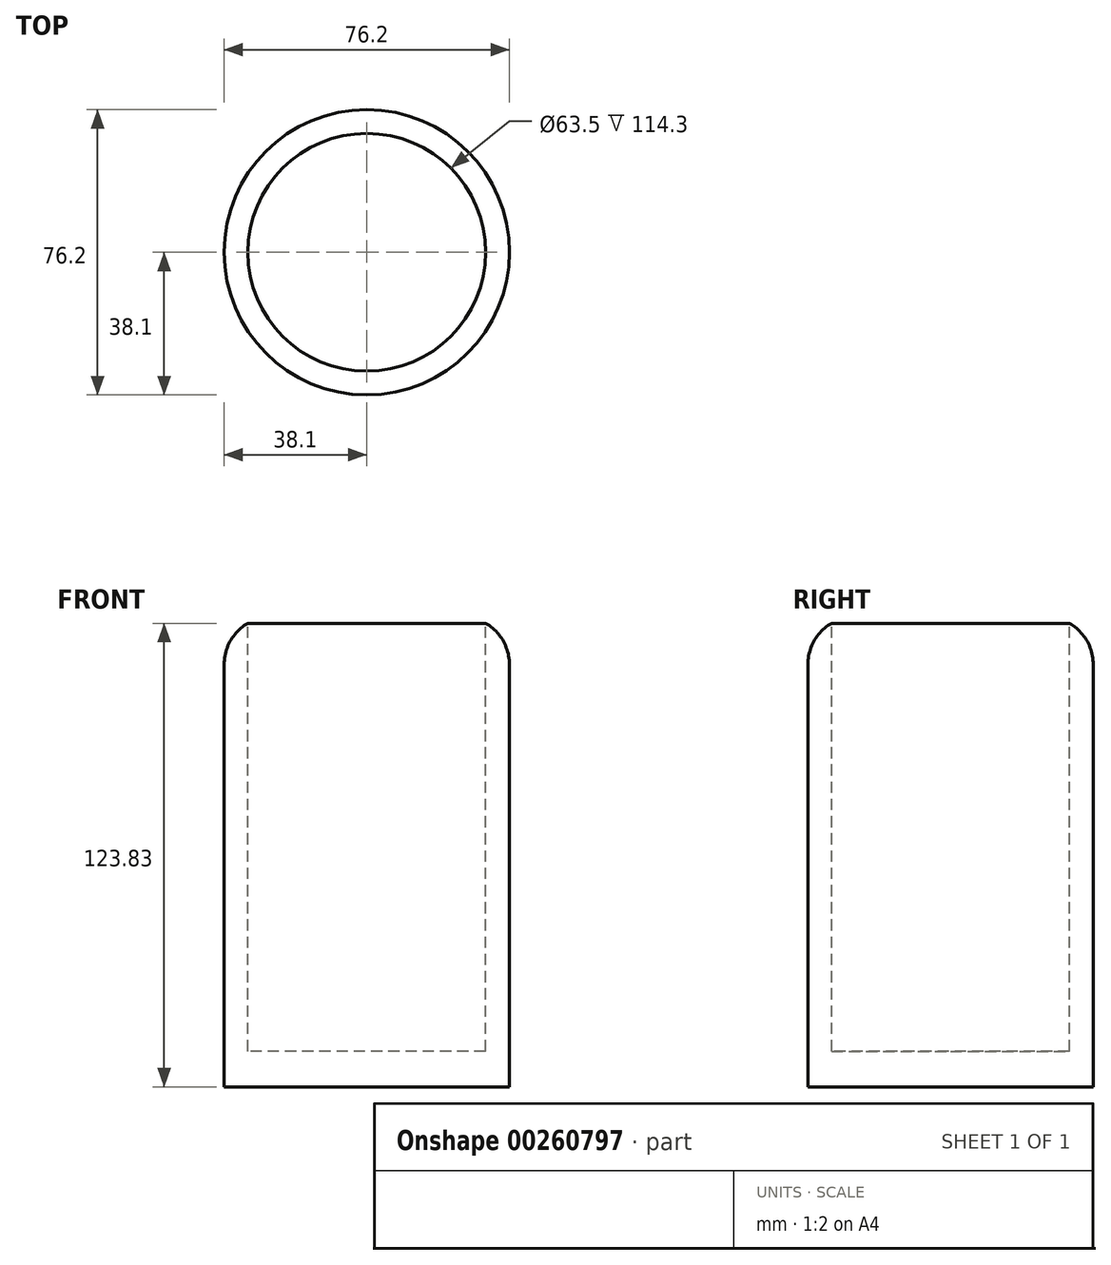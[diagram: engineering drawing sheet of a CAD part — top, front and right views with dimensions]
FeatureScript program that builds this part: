
annotation { "Feature Type Name" : "Feature", "Feature Type Description" : "" }
export const myFeature = defineFeature(function(context is Context, id is Id, definition is map)
    precondition{}
    {
        {
            var Q0;
            Q0=qCreatedBy(makeId("Top.planeOp"),FACE);
            var sketch = newSketch(context, id + "F0", { "sketchPlane" : qUnion([Q0])});
            skCircle(sketch, "E0", {"center": v(0, 0) * mm, "radius": 38.1 * mm});
            skCircle(sketch, "E1", {"center": v(0, 0) * mm, "radius": 31.75 * mm});
            skSolve(sketch);
        }
        {
            var Q0;
            Q0=makeQuery(id+"F0.imprint","IMPRINT",FACE,{"disambiguationData":[TD([[makeQuery(id+"F0.imprint","IMPRINT",EDGE,{"derivedFrom":sQuery(id+"F0.wireOp",EDGE,"E1")}),1.0]])]});
            var Q1;
            Q1=makeQuery(id+"F0.imprint","IMPRINT",FACE,{"disambiguationData":[TD([[makeQuery(id+"F0.imprint","IMPRINT",EDGE,{"derivedFrom":sQuery(id+"F0.wireOp",EDGE,"E0")}),1.0]])]});
            extrude(context, id + "F1", {"entities" : qUnion([Q0, Q1]), "oppositeDirection" : true, "depth" : 123.82 * mm});
        }
        {
            var Q0;
            Q0=makeQuery(id+"F0.imprint","IMPRINT",FACE,{"disambiguationData":[TD([[makeQuery(id+"F0.imprint","IMPRINT",EDGE,{"derivedFrom":sQuery(id+"F0.wireOp",EDGE,"E1")}),1.0]])]});
            extrude(context, id + "F2", {"entities" : qUnion([Q0]), "operationType" : NewBodyOperationType.REMOVE, "oppositeDirection" : true, "depth" : 114.3 * mm});
        }
        {
            var Q0;
            Q0=makeQuery(id+"F1.opExtrude","CAP_EDGE",EDGE,{"disambiguationData":[OSD([sQuery(id+"F0.wireOp",EDGE,"E0")])],"isStart":true});
            fillet(context, id + "F3", {"entities" : qUnion([Q0]), "radius" : 12.7 * mm, "tangentPropagation" : true, "allowEdgeOverflow" : false});
        }
    });
